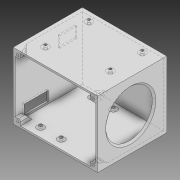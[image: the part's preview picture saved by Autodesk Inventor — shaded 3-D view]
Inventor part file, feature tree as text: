
AUTODESK INVENTOR PART (.ipt)
format: ipt  version: 2020 (Build 240168000, 168)  size: 304,128 bytes
history: native  units: mm
features: sketch x10, extrude x9, other x5, chamfer x2, projected_geometry x2, revolve x1, fillet x1
ambient origin geometry x8: Origin, YZ Plane, XZ Plane, XY Plane, X Axis, Y Axis, Z Axis, Center Point
bodies: Solid1 (feature_tree)
feature tree (30):
  other  "Blocks"
  extrude  "Extrusion1"  Depth=90.0mm
  extrude  "Extrusion2"  Depth=2.0mm TaperAngle=0.0deg
  revolve  "Revolution1"  [1 undecoded]
  extrude  "Extrusion3"  Depth=40.0mm
  extrude  "Extrusion4"  TaperAngle=90.0deg  [1 undecoded]
  extrude  "Extrusion5"  Depth=3.0mm
  extrude  "Extrusion6"  Depth=72.0mm TaperAngle=0.0deg
  chamfer  "Chamfer1"  Distance=2.0mm
  extrude  "Extrusion7"  Depth=2.0mm
  extrude  "Extrusion8"  Depth=15.0mm
  extrude  "Extrusion9"  Depth=45.0mm
  chamfer  "Chamfer2"  Distance=72.0mm
  fillet  "Fillet1"  Radius=8.0mm
  sketch  "Sketch1"  dims[d0=70.0mm d1=90.0mm]
  sketch  "Sketch2"  dims[d2=2.0mm d3=2.0mm d4=0.0mm]
  projected_geometry  "Projected Loop1"
  sketch  "Sketch3"  dims[d5=2.0mm d6=75.0mm d7=0.0mm]
  sketch  "Sketch4"  dims[d8=40.0mm d9=28.0mm]
  other  "Block1"
  sketch  "Sketch5"  dims[d10=45.0deg d11=90.0deg]
  sketch  "Sketch6"  dims[d12=59.5mm d13=66.5mm d14=54.8mm d15=48.5mm d16=16.0mm d17=2.7mm d20=3.0mm]
  other  "Block2"
  sketch  "Sketch7"  dims[d22=10.0mm d23=72.0mm d24=0.0mm]
  sketch  "Sketch8"  dims[d25=8.0mm d26=2.0mm d27=0.0mm]
  sketch  "Sketch9"  dims[d28=2.0mm d29=2.0mm d30=45.0deg]
  sketch  "Sketch10"  dims[d31=23.0mm d32=58.0mm d33=30.0mm d34=65.0mm d35=2.7mm d36=6.0mm d38=3.5mm d39=15.0mm d40=45.0mm d41=72.0mm d42=0.0mm d43=8.0mm d44=2.0mm d45=0.0mm d46=11.0mm d47=27.0mm d48=2.0mm d49=0.0mm d51=19.0mm d52=9.0mm d53=12.0mm d54=2.0mm d55=0.0mm d56=2.8mm d57=6.0mm d58=6.0mm d59=6.0mm d60=6.0mm d61=13.0mm d62=0.0mm d63=6.0mm d64=2.0mm d65=45.0deg d66=2.0mm]
  projected_geometry  "Projected Loop2"
  other  "Block1:1"
  other  "Block2:1"
note: 2 required parameter values undecoded (feature->parameter linkage not recoverable at this tier; creation-order binding heuristic only, values carry confidence <= 0.55)